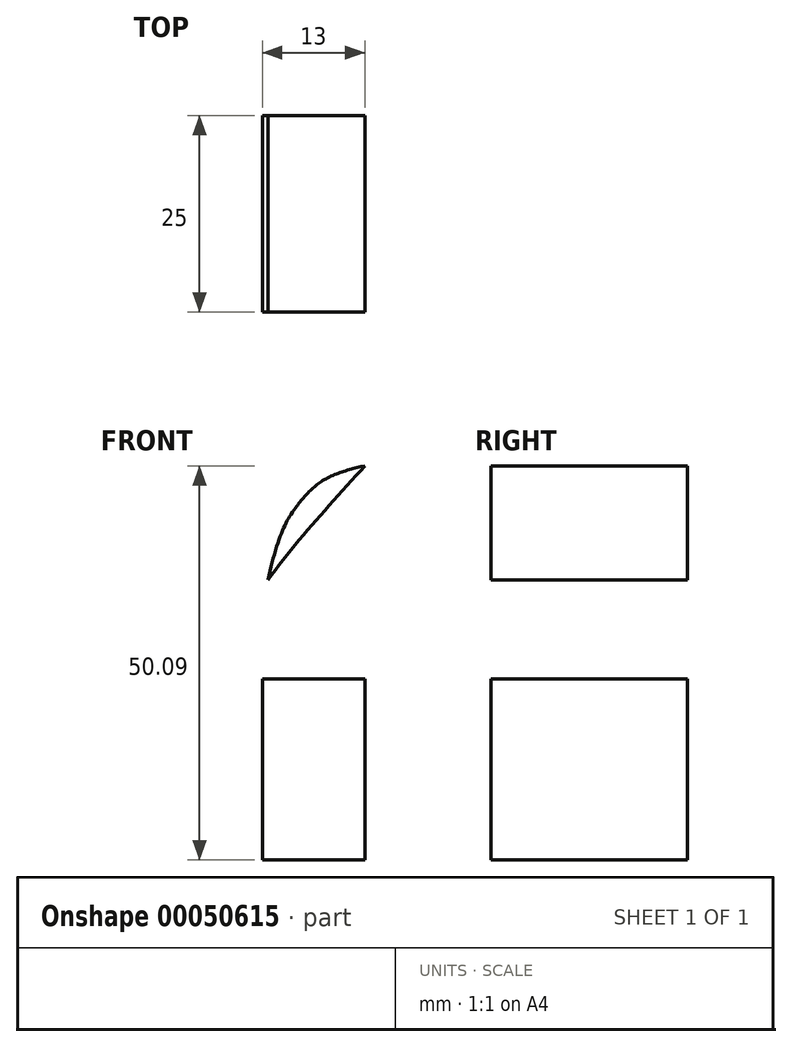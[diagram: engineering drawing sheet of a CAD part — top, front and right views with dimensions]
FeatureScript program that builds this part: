
annotation { "Feature Type Name" : "Feature", "Feature Type Description" : "" }
export const myFeature = defineFeature(function(context is Context, id is Id, definition is map)
    precondition{}
    {
        {
            var Q0;
            Q0=qCreatedBy(makeId("Front.planeOp"),FACE);
            var sketch = newSketch(context, id + "F0", { "sketchPlane" : qUnion([Q0])});
            skLineSegment(sketch, "E0", {"start": v(0, 0) * mm, "end": v(0, 23) * mm});
            skLineSegment(sketch, "E1", {"start": v(0, 0) * mm, "end": v(0, -23) * mm});
            skLineSegment(sketch, "E2", {"start": v(0, 0) * mm, "end": v(-13, 0) * mm});
            skLineSegment(sketch, "E3", {"start": v(-13, 0) * mm, "end": v(-13, 23) * mm});
            skLineSegment(sketch, "E4", {"start": v(-13, 23) * mm, "end": v(0, 23) * mm});
            skLineSegment(sketch, "E5", {"start": v(15.43, 23) * mm, "end": v(15.43, 49.46) * mm});
            skFitSpline(sketch, "E6", {"points": [v(-13, 23) * mm, v(-13, 31.5) * mm, v(-10.7, 41.26) * mm, v(-8.82, 44.73) * mm, v(-5.36, 48.2) * mm, v(0, 50.09) * mm], "startDerivative": vector(-2.27, 34.95) * mm, "endDerivative": vector(30.27, 7.22) * mm});
            skLineSegment(sketch, "E7", {"start": v(-4.22, -23) * mm, "end": v(-19.22, -23) * mm});
            skLineSegment(sketch, "E8", {"start": v(-19.22, -23) * mm, "end": v(-19.22, 0) * mm});
            skFitSpline(sketch, "E9", {"points": [v(-19.22, 0) * mm, v(-19.22, 23) * mm, v(0, 50.09) * mm], "startDerivative": vector(-8, 50.86) * mm, "endDerivative": vector(44.81, 49.36) * mm});
            skFitSpline(sketch, "E10", {"points": [v(-8.82, 44.73) * mm, v(-5.36, 48.2) * mm], "startDerivative": vector(3.46, 3.47) * mm, "endDerivative": vector(3.46, 3.47) * mm});
            skSolve(sketch);
        }
        {
            var Q0;
            Q0 = qSketchRegion(id + "F0", true);
            extrude(context, id + "F1", {"entities" : qUnion([Q0]), "depth" : 25 * mm});
        }
    });
